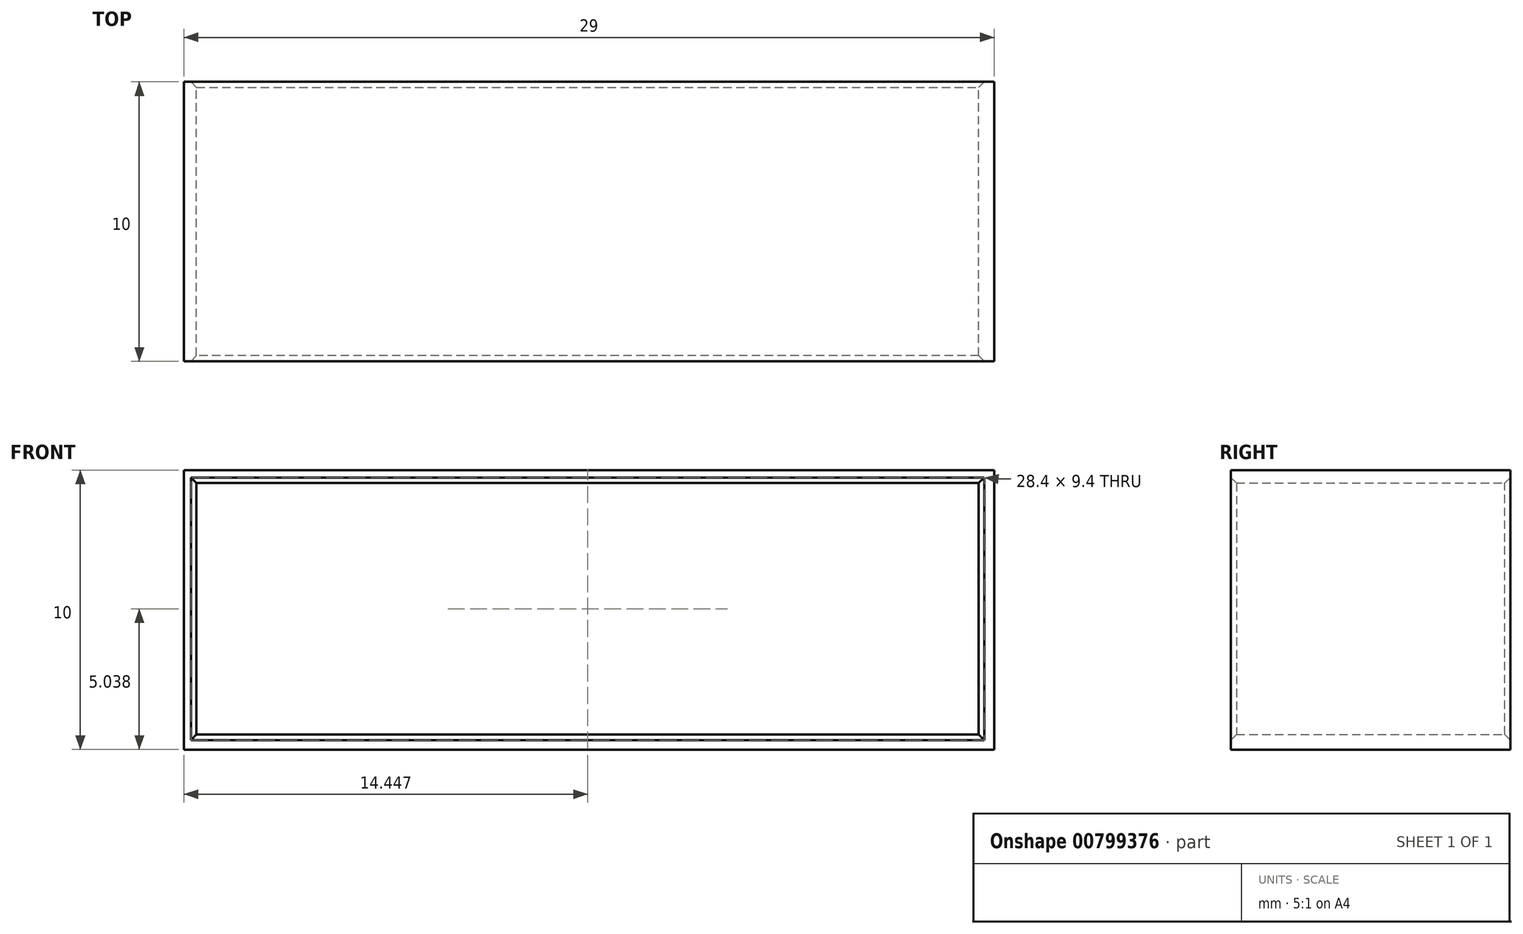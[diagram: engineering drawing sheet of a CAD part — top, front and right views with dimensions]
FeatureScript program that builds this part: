
annotation { "Feature Type Name" : "Feature", "Feature Type Description" : "" }
export const myFeature = defineFeature(function(context is Context, id is Id, definition is map)
    precondition{}
    {
        {
            var Q0;
            Q0=qCreatedBy(makeId("Front.planeOp"),FACE);
            var sketch = newSketch(context, id + "F0", { "sketchPlane" : qUnion([Q0])});
            skLineSegment(sketch, "E0.bottom", {"start": v(-23.07, 15.2) * mm, "end": v(5.93, 15.2) * mm});
            skLineSegment(sketch, "E0.top", {"start": v(-23.07, 5.2) * mm, "end": v(5.93, 5.2) * mm});
            skLineSegment(sketch, "E0.left", {"start": v(-23.07, 15.2) * mm, "end": v(-23.07, 5.2) * mm});
            skLineSegment(sketch, "E0.right", {"start": v(5.93, 15.2) * mm, "end": v(5.93, 5.2) * mm});
            skLineSegment(sketch, "E1.bottom", {"start": v(-22.62, 14.75) * mm, "end": v(5.38, 14.75) * mm});
            skLineSegment(sketch, "E1.top", {"start": v(-22.62, 5.75) * mm, "end": v(5.38, 5.75) * mm});
            skLineSegment(sketch, "E1.left", {"start": v(-22.62, 14.75) * mm, "end": v(-22.62, 5.75) * mm});
            skLineSegment(sketch, "E1.right", {"start": v(5.38, 14.75) * mm, "end": v(5.38, 5.75) * mm});
            skCircle(sketch, "E2", {"center": v(18.64, 3.69) * mm, "radius": 3.55 * mm});
            skCircle(sketch, "E3", {"center": v(18.64, 3.69) * mm, "radius": 2.97 * mm});
            skSolve(sketch);
        }
        {
            var Q0;
            Q0=makeQuery(id+"F0.imprint","IMPRINT",FACE,{"disambiguationData":[TD([[makeQuery(id+"F0.imprint","IMPRINT",EDGE,{"derivedFrom":sQuery(id+"F0.wireOp",EDGE,"E0.bottom")}),-1.0]])]});
            extrude(context, id + "F1", {"entities" : qUnion([Q0]), "depth" : 10 * mm, "offsetDistance" : 25 * mm});
        }
        {
            var Q0;
            Q0=makeQuery(id+"F1.opExtrude","CAP_EDGE",EDGE,{"disambiguationData":[OSD([sQuery(id+"F0.wireOp",EDGE,"E1.top")])],"isStart":false});
            var Q1;
            Q1=makeQuery(id+"F1.opExtrude","CAP_EDGE",EDGE,{"disambiguationData":[OSD([sQuery(id+"F0.wireOp",EDGE,"E1.bottom")])],"isStart":false});
            var Q2;
            Q2=makeQuery(id+"F1.opExtrude","CAP_EDGE",EDGE,{"disambiguationData":[OSD([sQuery(id+"F0.wireOp",EDGE,"E1.right")])],"isStart":false});
            var Q3;
            Q3=makeQuery(id+"F1.opExtrude","CAP_EDGE",EDGE,{"disambiguationData":[OSD([sQuery(id+"F0.wireOp",EDGE,"E1.left")])],"isStart":false});
            var Q4;
            Q4=makeQuery(id+"F1.opExtrude","CAP_EDGE",EDGE,{"disambiguationData":[OSD([sQuery(id+"F0.wireOp",EDGE,"E1.left")])],"isStart":true});
            var Q5;
            Q5=makeQuery(id+"F1.opExtrude","CAP_EDGE",EDGE,{"disambiguationData":[OSD([sQuery(id+"F0.wireOp",EDGE,"E1.bottom")])],"isStart":true});
            var Q6;
            Q6=makeQuery(id+"F1.opExtrude","CAP_EDGE",EDGE,{"disambiguationData":[OSD([sQuery(id+"F0.wireOp",EDGE,"E1.top")])],"isStart":true});
            var Q7;
            Q7=makeQuery(id+"F1.opExtrude","CAP_EDGE",EDGE,{"disambiguationData":[OSD([sQuery(id+"F0.wireOp",EDGE,"E1.right")])],"isStart":true});
            chamfer(context, id + "F2", {"entities" : qUnion([Q0, Q1, Q2, Q3, Q4, Q5, Q6, Q7]), "width" : .2 * mm, "tangentPropagation" : true});
        }
    });
